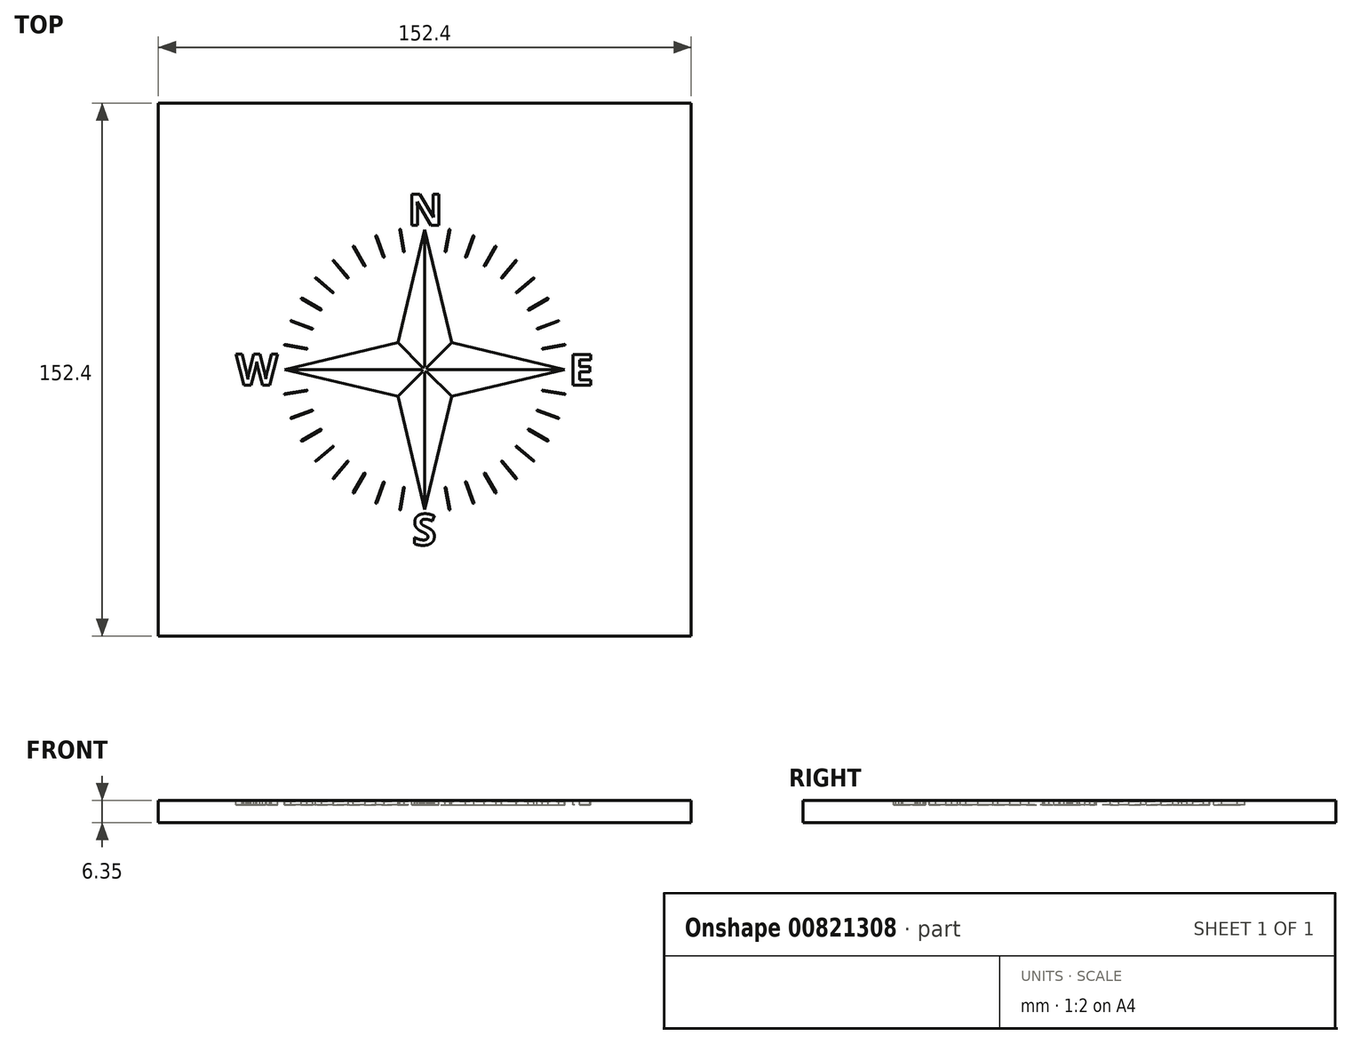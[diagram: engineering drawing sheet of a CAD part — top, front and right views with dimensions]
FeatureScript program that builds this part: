
annotation { "Feature Type Name" : "Feature", "Feature Type Description" : "" }
export const myFeature = defineFeature(function(context is Context, id is Id, definition is map)
    precondition{}
    {
        {
            var Q0;
            Q0=qCreatedBy(makeId("Top.planeOp"),FACE);
            var sketch = newSketch(context, id + "F0", { "sketchPlane" : qUnion([Q0])});
            skLineSegment(sketch, "E0.bottom", {"start": v(0, 0) * mm, "end": v(152.4, 0) * mm});
            skLineSegment(sketch, "E0.top", {"start": v(0, 152.4) * mm, "end": v(152.4, 152.4) * mm});
            skLineSegment(sketch, "E0.left", {"start": v(0, 0) * mm, "end": v(0, 152.4) * mm});
            skLineSegment(sketch, "E0.right", {"start": v(152.4, 0) * mm, "end": v(152.4, 152.4) * mm});
            skSolve(sketch);
        }
        {
            var Q0;
            Q0=makeQuery(id+"F0.imprint","IMPRINT",FACE,{"disambiguationData":[TD([[makeQuery(id+"F0.imprint","IMPRINT",EDGE,{"derivedFrom":sQuery(id+"F0.wireOp",EDGE,"E0.bottom")}),1.0]])]});
            extrude(context, id + "F1", {"entities" : qUnion([Q0]), "depth" : 6.35 * mm, "offsetDistance" : 25.4 * mm});
        }
        {
            var Q0;
            Q0=makeQuery(id+"F1.opExtrude","CAP_FACE",FACE,{"disambiguationData":[OSD([sQuery(id+"F0.wireOp",EDGE,"E0.bottom"),sQuery(id+"F0.wireOp",EDGE,"E0.top"),sQuery(id+"F0.wireOp",EDGE,"E0.left"),sQuery(id+"F0.wireOp",EDGE,"E0.right")])],"isStart":false});
            var sketch = newSketch(context, id + "F2", { "sketchPlane" : qUnion([Q0])});
            skCircle(sketch, "E1", {"center": v(76.2, 76.2) * mm, "radius": 38.1 * mm, "construction": true});
            skPoint(sketch, "E1.centerSnap0", {"position": v(76.2, 152.4) * mm});
            skPoint(sketch, "E1.centerSnap1", {"position": v(0, 76.2) * mm});
            skText(sketch, "E2", { "text": "N", "fontName": "OpenSans-Bold.ttf"});
            skText(sketch, "E3", { "text": "E", "fontName": "OpenSans-Bold.ttf"});
            skText(sketch, "E4", { "text": "S", "fontName": "OpenSans-Bold.ttf"});
            skText(sketch, "E5", { "text": "W", "fontName": "OpenSans-Bold.ttf"});
            skPoint(sketch, "E6", {"position": v(34.92, 76.2) * mm});
            skPoint(sketch, "E7", {"position": v(117.48, 76.2) * mm});
            const initialGuessF2  = {"E2": [0.07134, 0.11748, 1, 0, 0.0089], "E3": [0.11747, 0.07175, 1, 0, 0.00889], "E4": [0.07264, 0.02604, 1, 0, 0.0089], "E5": [0.02219, 0.07176, 1, 0, 0.00889]};
            skSetInitialGuess(sketch, initialGuessF2);
            skSolve(sketch);
        }
        {
            var Q0;
            Q0=makeQuery(id+"F2.imprint","IMPRINT",FACE,{"disambiguationData":[TD([[makeQuery(id+"F2.imprint","IMPRINT",EDGE,{"derivedFrom":sQuery(id+"F2.wireOp",EDGE,"E2.sketch_text.stroke-0")}),-1.0]])]});
            var Q1;
            Q1=makeQuery(id+"F2.imprint","IMPRINT",FACE,{"disambiguationData":[TD([[makeQuery(id+"F2.imprint","IMPRINT",EDGE,{"derivedFrom":sQuery(id+"F2.wireOp",EDGE,"E3.sketch_text.stroke-0")}),-1.0]])]});
            var Q2;
            Q2=makeQuery(id+"F2.imprint","IMPRINT",FACE,{"disambiguationData":[TD([[makeQuery(id+"F2.imprint","IMPRINT",EDGE,{"derivedFrom":sQuery(id+"F2.wireOp",EDGE,"E4.sketch_text.stroke-0")}),-1.0]])]});
            var Q3;
            Q3=makeQuery(id+"F2.imprint","IMPRINT",FACE,{"disambiguationData":[TD([[makeQuery(id+"F2.imprint","IMPRINT",EDGE,{"derivedFrom":sQuery(id+"F2.wireOp",EDGE,"E5.sketch_text.stroke-0")}),-1.0]])]});
            extrude(context, id + "F3", {"entities" : qUnion([Q0, Q1, Q2, Q3]), "operationType" : NewBodyOperationType.REMOVE, "oppositeDirection" : true, "depth" : 1.27 * mm, "offsetDistance" : 25.4 * mm});
        }
        {
            var Q0;
            Q0=makeQuery(id+"F1.opExtrude","CAP_FACE",FACE,{"disambiguationData":[OSD([sQuery(id+"F0.wireOp",EDGE,"E0.bottom"),sQuery(id+"F0.wireOp",EDGE,"E0.top"),sQuery(id+"F0.wireOp",EDGE,"E0.left"),sQuery(id+"F0.wireOp",EDGE,"E0.right")])],"isStart":false});
            var sketch = newSketch(context, id + "F4", { "sketchPlane" : qUnion([Q0])});
            skLineSegment(sketch, "E8", {"start": v(0, 76.2) * mm, "end": v(152.4, 76.2) * mm, "construction": true});
            skCircle(sketch, "E9", {"center": v(76.2, 76.2) * mm, "radius": 38.1 * mm, "construction": true});
            skCircle(sketch, "E10", {"center": v(76.2, 76.2) * mm, "radius": 40 * mm});
            skLineSegment(sketch, "E11", {"start": v(76.2, 116.2) * mm, "end": v(68.5, 83.9) * mm});
            skLineSegment(sketch, "E12", {"start": v(68.5, 68.5) * mm, "end": v(76.2, 36.2) * mm});
            skLineSegment(sketch, "E13", {"start": v(76.2, 36.2) * mm, "end": v(83.9, 68.5) * mm});
            skLineSegment(sketch, "E14", {"start": v(83.9, 83.9) * mm, "end": v(76.2, 116.2) * mm});
            skLineSegment(sketch, "E15", {"start": v(36.2, 76.2) * mm, "end": v(68.5, 83.9) * mm});
            skLineSegment(sketch, "E16", {"start": v(83.9, 83.9) * mm, "end": v(116.2, 76.2) * mm});
            skLineSegment(sketch, "E17", {"start": v(116.2, 76.2) * mm, "end": v(83.9, 68.5) * mm});
            skLineSegment(sketch, "E18", {"start": v(68.5, 68.5) * mm, "end": v(36.2, 76.2) * mm});
            skPoint(sketch, "E19.orphan", {"position": v(76.2, 85.72) * mm});
            skPoint(sketch, "E20.orphan", {"position": v(85.73, 76.2) * mm});
            skPoint(sketch, "E21.orphan", {"position": v(76.2, 66.67) * mm});
            skPoint(sketch, "E22.orphan", {"position": v(66.67, 76.2) * mm});
            skSolve(sketch);
        }
        {
            var Q0;
            Q0=makeQuery(id+"F4.imprint","IMPRINT",FACE,{"disambiguationData":[TD([[makeQuery(id+"F4.imprint","IMPRINT",EDGE,{"derivedFrom":sQuery(id+"F4.wireOp",EDGE,"E11")}),1.0]])]});
            extrude(context, id + "F5", {"entities" : qUnion([Q0]), "operationType" : NewBodyOperationType.REMOVE, "oppositeDirection" : true, "depth" : 1.27 * mm, "offsetDistance" : 25.4 * mm});
        }
        {
            var Q0;
            Q0=makeQuery(id+"F5.boolean.opBoolean","COPY",FACE,{"derivedFrom":makeQuery(id+"F5.opExtrude","CAP_FACE",FACE,{"disambiguationData":[OSD([sQuery(id+"F4.wireOp",EDGE,"E11"),sQuery(id+"F4.wireOp",EDGE,"E12"),sQuery(id+"F4.wireOp",EDGE,"E13"),sQuery(id+"F4.wireOp",EDGE,"E14"),sQuery(id+"F4.wireOp",EDGE,"E15"),sQuery(id+"F4.wireOp",EDGE,"E16"),sQuery(id+"F4.wireOp",EDGE,"E17"),sQuery(id+"F4.wireOp",EDGE,"E18")])],"isStart":false})});
            var sketch = newSketch(context, id + "F6", { "sketchPlane" : qUnion([Q0])});
            skLineSegment(sketch, "E23.0.0", {"start": v(68.5, 68.5) * mm, "end": v(76.2, 36.2) * mm});
            skLineSegment(sketch, "E23.0.1", {"start": v(76.2, 36.2) * mm, "end": v(83.9, 68.5) * mm});
            skLineSegment(sketch, "E23.0.2", {"start": v(83.9, 68.5) * mm, "end": v(116.2, 76.2) * mm});
            skLineSegment(sketch, "E23.0.3", {"start": v(116.2, 76.2) * mm, "end": v(83.9, 83.9) * mm});
            skLineSegment(sketch, "E23.0.4", {"start": v(83.9, 83.9) * mm, "end": v(76.2, 116.2) * mm});
            skLineSegment(sketch, "E23.0.5", {"start": v(76.2, 116.2) * mm, "end": v(68.5, 83.9) * mm});
            skLineSegment(sketch, "E23.0.6", {"start": v(68.5, 83.9) * mm, "end": v(36.2, 76.2) * mm});
            skLineSegment(sketch, "E23.0.7", {"start": v(36.2, 76.2) * mm, "end": v(68.5, 68.5) * mm});
            skLineSegment(sketch, "E24", {"start": v(76.2, 116.2) * mm, "end": v(76.2, 76.96) * mm});
            skLineSegment(sketch, "E25", {"start": v(36.2, 76.2) * mm, "end": v(75.44, 76.2) * mm});
            skLineSegment(sketch, "E26", {"start": v(68.5, 83.9) * mm, "end": v(75.66, 76.74) * mm});
            skLineSegment(sketch, "E27", {"start": v(83.9, 83.9) * mm, "end": v(76.74, 76.74) * mm});
            skCircle(sketch, "E28", {"center": v(76.2, 76.2) * mm, "radius": 0.76 * mm});
            skLineSegment(sketch, "E29.trimOffspring", {"start": v(76.74, 75.66) * mm, "end": v(83.9, 68.5) * mm});
            skLineSegment(sketch, "E30.trimOffspring", {"start": v(76.96, 76.2) * mm, "end": v(116.2, 76.2) * mm});
            skLineSegment(sketch, "E31.trimOffspring", {"start": v(75.66, 75.66) * mm, "end": v(68.5, 68.5) * mm});
            skLineSegment(sketch, "E32.trimOffspring", {"start": v(76.2, 75.44) * mm, "end": v(76.2, 36.2) * mm});
            skSolve(sketch);
        }
        {
            var Q0;
            Q0=makeQuery(id+"F6.imprint","IMPRINT",FACE,{"disambiguationData":[TD([[makeQuery(id+"F6.imprint","IMPRINT",EDGE,{"derivedFrom":sQuery(id+"F6.wireOp",EDGE,"E23.0.4")}),1.0]])]});
            var Q1;
            Q1=makeQuery(id+"F6.imprint","IMPRINT",FACE,{"disambiguationData":[TD([[makeQuery(id+"F6.imprint","IMPRINT",EDGE,{"derivedFrom":sQuery(id+"F6.wireOp",EDGE,"E23.0.6")}),-1.0]])]});
            var Q2;
            Q2=makeQuery(id+"F6.imprint","IMPRINT",FACE,{"disambiguationData":[TD([[makeQuery(id+"F6.imprint","IMPRINT",EDGE,{"derivedFrom":sQuery(id+"F6.wireOp",EDGE,"E23.0.0")}),1.0]])]});
            var Q3;
            Q3=makeQuery(id+"F6.imprint","IMPRINT",FACE,{"disambiguationData":[TD([[makeQuery(id+"F6.imprint","IMPRINT",EDGE,{"derivedFrom":sQuery(id+"F6.wireOp",EDGE,"E23.0.2")}),-1.0]])]});
            var Q4;
            {var subQ0=sQuery(id+"F6.wireOp",EDGE,"E28");var subQ4=makeQuery(id+"F6.imprint","INTERSECT",VERTEX,{"derivedFrom":[sQuery(id+"F6.wireOp",EDGE,"E27"),subQ0]});Q4=makeQuery(id+"F6.imprint","IMPRINT",FACE,{"disambiguationData":[TD([[makeQuery(id+"F6.imprint","IMPRINT",EDGE,{"disambiguationData":[TD([[subQ4,1.0]])],"derivedFrom":subQ0}),1.0]])]});}
            extrude(context, id + "F7", {"entities" : qUnion([Q0, Q1, Q2, Q3, Q4]), "operationType" : NewBodyOperationType.ADD, "depth" : 1.02 * mm, "offsetDistance" : 25.4 * mm});
        }
        {
            var Q0;
            Q0=makeQuery(id+"F1.opExtrude","CAP_FACE",FACE,{"disambiguationData":[OSD([sQuery(id+"F0.wireOp",EDGE,"E0.bottom"),sQuery(id+"F0.wireOp",EDGE,"E0.top"),sQuery(id+"F0.wireOp",EDGE,"E0.left"),sQuery(id+"F0.wireOp",EDGE,"E0.right")])],"isStart":false});
            var sketch = newSketch(context, id + "F8", { "sketchPlane" : qUnion([Q0])});
            skLineSegment(sketch, "E33.0", {"start": v(36.2, 76.2) * mm, "end": v(75.44, 76.2) * mm});
            skLineSegment(sketch, "E34.0", {"start": v(76.96, 76.2) * mm, "end": v(116.2, 76.2) * mm});
            skLineSegment(sketch, "E35.0", {"start": v(76.2, 75.44) * mm, "end": v(76.2, 36.2) * mm});
            skPoint(sketch, "E36", {"position": v(76.2, 76.2) * mm});
            skCircle(sketch, "E37", {"center": v(76.2, 76.2) * mm, "radius": 37.07 * mm, "construction": true});
            skCircle(sketch, "E38", {"center": v(76.2, 76.2) * mm, "radius": 37.84 * mm, "construction": true});
            skLineSegment(sketch, "E39", {"start": v(76.07, 110.48) * mm, "end": v(76.07, 116.83) * mm});
            skLineSegment(sketch, "E40", {"start": v(76.33, 110.48) * mm, "end": v(76.33, 116.83) * mm});
            skArc(sketch, "E41", {"start": v(76.33, 116.83) * mm, "mid": v(76.2, 116.96) * mm, "end": v(76.07, 116.83) * mm});
            skArc(sketch, "E42", {"start": v(76.07, 110.48) * mm, "mid": v(76.2, 110.35) * mm, "end": v(76.33, 110.48) * mm});
            skLineSegment(sketch, "E43", {"start": v(76.2, 113.27) * mm, "end": v(76.2, 114.04) * mm, "construction": true});
            skPoint(sketch, "E43.startSnap0", {"position": v(76.2, 110.35) * mm});
            skPoint(sketch, "E44", {"position": v(76.2, 113.65) * mm});
            skLineSegment(sketch, "E45.1.0", {"start": v(70.12, 109.94) * mm, "end": v(69.02, 116.19) * mm});
            skLineSegment(sketch, "E45.1.1", {"start": v(70.37, 109.98) * mm, "end": v(69.27, 116.23) * mm});
            skArc(sketch, "E45.1.2", {"start": v(70.12, 109.94) * mm, "mid": v(70.27, 109.83) * mm, "end": v(70.37, 109.98) * mm});
            skArc(sketch, "E45.1.3", {"start": v(69.27, 116.23) * mm, "mid": v(69.12, 116.34) * mm, "end": v(69.02, 116.19) * mm});
            skLineSegment(sketch, "E45.2.0", {"start": v(64.36, 108.37) * mm, "end": v(62.18, 114.34) * mm});
            skLineSegment(sketch, "E45.2.1", {"start": v(64.6, 108.46) * mm, "end": v(62.42, 114.42) * mm});
            skArc(sketch, "E45.2.2", {"start": v(64.36, 108.37) * mm, "mid": v(64.52, 108.3) * mm, "end": v(64.6, 108.46) * mm});
            skArc(sketch, "E45.2.3", {"start": v(62.42, 114.42) * mm, "mid": v(62.26, 114.5) * mm, "end": v(62.18, 114.34) * mm});
            skLineSegment(sketch, "E45.3.0", {"start": v(58.95, 105.82) * mm, "end": v(55.78, 111.32) * mm});
            skLineSegment(sketch, "E45.3.1", {"start": v(59.17, 105.95) * mm, "end": v(56, 111.45) * mm});
            skArc(sketch, "E45.3.2", {"start": v(58.95, 105.82) * mm, "mid": v(59.12, 105.78) * mm, "end": v(59.17, 105.95) * mm});
            skArc(sketch, "E45.3.3", {"start": v(56, 111.45) * mm, "mid": v(55.82, 111.5) * mm, "end": v(55.78, 111.32) * mm});
            skLineSegment(sketch, "E45.4.0", {"start": v(54.07, 102.38) * mm, "end": v(49.99, 107.24) * mm});
            skLineSegment(sketch, "E45.4.1", {"start": v(54.26, 102.54) * mm, "end": v(50.18, 107.4) * mm});
            skArc(sketch, "E45.4.2", {"start": v(54.07, 102.38) * mm, "mid": v(54.25, 102.36) * mm, "end": v(54.26, 102.54) * mm});
            skArc(sketch, "E45.4.3", {"start": v(50.18, 107.4) * mm, "mid": v(50, 107.42) * mm, "end": v(49.99, 107.24) * mm});
            skLineSegment(sketch, "E45.5.0", {"start": v(49.86, 98.14) * mm, "end": v(45, 102.22) * mm});
            skLineSegment(sketch, "E45.5.1", {"start": v(50.02, 98.33) * mm, "end": v(45.16, 102.41) * mm});
            skArc(sketch, "E45.5.2", {"start": v(49.86, 98.14) * mm, "mid": v(50.04, 98.15) * mm, "end": v(50.02, 98.33) * mm});
            skArc(sketch, "E45.5.3", {"start": v(45.16, 102.41) * mm, "mid": v(44.98, 102.4) * mm, "end": v(45, 102.22) * mm});
            skLineSegment(sketch, "E45.6.0", {"start": v(46.45, 93.23) * mm, "end": v(40.95, 96.4) * mm});
            skLineSegment(sketch, "E45.6.1", {"start": v(46.58, 93.45) * mm, "end": v(41.08, 96.62) * mm});
            skArc(sketch, "E45.6.2", {"start": v(46.45, 93.23) * mm, "mid": v(46.62, 93.28) * mm, "end": v(46.58, 93.45) * mm});
            skArc(sketch, "E45.6.3", {"start": v(41.08, 96.62) * mm, "mid": v(40.9, 96.58) * mm, "end": v(40.95, 96.4) * mm});
            skLineSegment(sketch, "E45.7.0", {"start": v(43.94, 87.8) * mm, "end": v(37.98, 89.98) * mm});
            skLineSegment(sketch, "E45.7.1", {"start": v(44.03, 88.04) * mm, "end": v(38.06, 90.22) * mm});
            skArc(sketch, "E45.7.2", {"start": v(43.94, 87.8) * mm, "mid": v(44.1, 87.88) * mm, "end": v(44.03, 88.04) * mm});
            skArc(sketch, "E45.7.3", {"start": v(38.06, 90.22) * mm, "mid": v(37.9, 90.14) * mm, "end": v(37.98, 89.98) * mm});
            skLineSegment(sketch, "E45.8.0", {"start": v(42.42, 82.03) * mm, "end": v(36.17, 83.13) * mm});
            skLineSegment(sketch, "E45.8.1", {"start": v(42.46, 82.28) * mm, "end": v(36.21, 83.38) * mm});
            skArc(sketch, "E45.8.2", {"start": v(42.42, 82.03) * mm, "mid": v(42.57, 82.13) * mm, "end": v(42.46, 82.28) * mm});
            skArc(sketch, "E45.8.3", {"start": v(36.21, 83.38) * mm, "mid": v(36.06, 83.28) * mm, "end": v(36.17, 83.13) * mm});
            skLineSegment(sketch, "E45.9.0", {"start": v(41.92, 76.07) * mm, "end": v(35.57, 76.07) * mm});
            skLineSegment(sketch, "E45.9.1", {"start": v(41.92, 76.33) * mm, "end": v(35.57, 76.33) * mm});
            skArc(sketch, "E45.9.2", {"start": v(41.92, 76.07) * mm, "mid": v(42.05, 76.2) * mm, "end": v(41.92, 76.33) * mm});
            skArc(sketch, "E45.9.3", {"start": v(35.57, 76.33) * mm, "mid": v(35.44, 76.2) * mm, "end": v(35.57, 76.07) * mm});
            skLineSegment(sketch, "E45.10.0", {"start": v(42.46, 70.12) * mm, "end": v(36.21, 69.02) * mm});
            skLineSegment(sketch, "E45.10.1", {"start": v(42.42, 70.37) * mm, "end": v(36.17, 69.27) * mm});
            skArc(sketch, "E45.10.2", {"start": v(42.46, 70.12) * mm, "mid": v(42.57, 70.27) * mm, "end": v(42.42, 70.37) * mm});
            skArc(sketch, "E45.10.3", {"start": v(36.17, 69.27) * mm, "mid": v(36.06, 69.12) * mm, "end": v(36.21, 69.02) * mm});
            skLineSegment(sketch, "E45.11.0", {"start": v(44.03, 64.36) * mm, "end": v(38.06, 62.18) * mm});
            skLineSegment(sketch, "E45.11.1", {"start": v(43.94, 64.6) * mm, "end": v(37.98, 62.42) * mm});
            skArc(sketch, "E45.11.2", {"start": v(44.03, 64.36) * mm, "mid": v(44.1, 64.52) * mm, "end": v(43.94, 64.6) * mm});
            skArc(sketch, "E45.11.3", {"start": v(37.98, 62.42) * mm, "mid": v(37.9, 62.26) * mm, "end": v(38.06, 62.18) * mm});
            skLineSegment(sketch, "E45.12.0", {"start": v(46.58, 58.95) * mm, "end": v(41.08, 55.78) * mm});
            skLineSegment(sketch, "E45.12.1", {"start": v(46.45, 59.17) * mm, "end": v(40.95, 56) * mm});
            skArc(sketch, "E45.12.2", {"start": v(46.58, 58.95) * mm, "mid": v(46.62, 59.12) * mm, "end": v(46.45, 59.17) * mm});
            skArc(sketch, "E45.12.3", {"start": v(40.95, 56) * mm, "mid": v(40.9, 55.82) * mm, "end": v(41.08, 55.78) * mm});
            skLineSegment(sketch, "E45.13.0", {"start": v(50.02, 54.07) * mm, "end": v(45.16, 49.99) * mm});
            skLineSegment(sketch, "E45.13.1", {"start": v(49.86, 54.26) * mm, "end": v(45, 50.18) * mm});
            skArc(sketch, "E45.13.2", {"start": v(50.02, 54.07) * mm, "mid": v(50.04, 54.25) * mm, "end": v(49.86, 54.26) * mm});
            skArc(sketch, "E45.13.3", {"start": v(45, 50.18) * mm, "mid": v(44.98, 50) * mm, "end": v(45.16, 49.99) * mm});
            skLineSegment(sketch, "E45.14.0", {"start": v(54.26, 49.86) * mm, "end": v(50.18, 45) * mm});
            skLineSegment(sketch, "E45.14.1", {"start": v(54.07, 50.02) * mm, "end": v(49.99, 45.16) * mm});
            skArc(sketch, "E45.14.2", {"start": v(54.26, 49.86) * mm, "mid": v(54.25, 50.04) * mm, "end": v(54.07, 50.02) * mm});
            skArc(sketch, "E45.14.3", {"start": v(49.99, 45.16) * mm, "mid": v(50, 44.98) * mm, "end": v(50.18, 45) * mm});
            skLineSegment(sketch, "E45.15.0", {"start": v(59.17, 46.45) * mm, "end": v(56, 40.95) * mm});
            skLineSegment(sketch, "E45.15.1", {"start": v(58.95, 46.58) * mm, "end": v(55.78, 41.08) * mm});
            skArc(sketch, "E45.15.2", {"start": v(59.17, 46.45) * mm, "mid": v(59.12, 46.62) * mm, "end": v(58.95, 46.58) * mm});
            skArc(sketch, "E45.15.3", {"start": v(55.78, 41.08) * mm, "mid": v(55.82, 40.9) * mm, "end": v(56, 40.95) * mm});
            skLineSegment(sketch, "E45.16.0", {"start": v(64.6, 43.94) * mm, "end": v(62.42, 37.98) * mm});
            skLineSegment(sketch, "E45.16.1", {"start": v(64.36, 44.03) * mm, "end": v(62.18, 38.06) * mm});
            skArc(sketch, "E45.16.2", {"start": v(64.6, 43.94) * mm, "mid": v(64.52, 44.1) * mm, "end": v(64.36, 44.03) * mm});
            skArc(sketch, "E45.16.3", {"start": v(62.18, 38.06) * mm, "mid": v(62.26, 37.9) * mm, "end": v(62.42, 37.98) * mm});
            skLineSegment(sketch, "E45.17.0", {"start": v(70.37, 42.42) * mm, "end": v(69.27, 36.17) * mm});
            skLineSegment(sketch, "E45.17.1", {"start": v(70.12, 42.46) * mm, "end": v(69.02, 36.21) * mm});
            skArc(sketch, "E45.17.2", {"start": v(70.37, 42.42) * mm, "mid": v(70.27, 42.57) * mm, "end": v(70.12, 42.46) * mm});
            skArc(sketch, "E45.17.3", {"start": v(69.02, 36.21) * mm, "mid": v(69.12, 36.06) * mm, "end": v(69.27, 36.17) * mm});
            skLineSegment(sketch, "E45.18.0", {"start": v(76.33, 41.92) * mm, "end": v(76.33, 35.57) * mm});
            skLineSegment(sketch, "E45.18.1", {"start": v(76.07, 41.92) * mm, "end": v(76.07, 35.57) * mm});
            skArc(sketch, "E45.18.2", {"start": v(76.33, 41.92) * mm, "mid": v(76.2, 42.05) * mm, "end": v(76.07, 41.92) * mm});
            skArc(sketch, "E45.18.3", {"start": v(76.07, 35.57) * mm, "mid": v(76.2, 35.44) * mm, "end": v(76.33, 35.57) * mm});
            skLineSegment(sketch, "E45.19.0", {"start": v(82.28, 42.46) * mm, "end": v(83.38, 36.21) * mm});
            skLineSegment(sketch, "E45.19.1", {"start": v(82.03, 42.42) * mm, "end": v(83.13, 36.17) * mm});
            skArc(sketch, "E45.19.2", {"start": v(82.28, 42.46) * mm, "mid": v(82.13, 42.57) * mm, "end": v(82.03, 42.42) * mm});
            skArc(sketch, "E45.19.3", {"start": v(83.13, 36.17) * mm, "mid": v(83.28, 36.06) * mm, "end": v(83.38, 36.21) * mm});
            skLineSegment(sketch, "E45.20.0", {"start": v(88.04, 44.03) * mm, "end": v(90.22, 38.06) * mm});
            skLineSegment(sketch, "E45.20.1", {"start": v(87.8, 43.94) * mm, "end": v(89.98, 37.98) * mm});
            skArc(sketch, "E45.20.2", {"start": v(88.04, 44.03) * mm, "mid": v(87.88, 44.1) * mm, "end": v(87.8, 43.94) * mm});
            skArc(sketch, "E45.20.3", {"start": v(89.98, 37.98) * mm, "mid": v(90.14, 37.9) * mm, "end": v(90.22, 38.06) * mm});
            skLineSegment(sketch, "E45.21.0", {"start": v(93.45, 46.58) * mm, "end": v(96.62, 41.08) * mm});
            skLineSegment(sketch, "E45.21.1", {"start": v(93.23, 46.45) * mm, "end": v(96.4, 40.95) * mm});
            skArc(sketch, "E45.21.2", {"start": v(93.45, 46.58) * mm, "mid": v(93.28, 46.62) * mm, "end": v(93.23, 46.45) * mm});
            skArc(sketch, "E45.21.3", {"start": v(96.4, 40.95) * mm, "mid": v(96.58, 40.9) * mm, "end": v(96.62, 41.08) * mm});
            skLineSegment(sketch, "E45.22.0", {"start": v(98.33, 50.02) * mm, "end": v(102.41, 45.16) * mm});
            skLineSegment(sketch, "E45.22.1", {"start": v(98.14, 49.86) * mm, "end": v(102.22, 45) * mm});
            skArc(sketch, "E45.22.2", {"start": v(98.33, 50.02) * mm, "mid": v(98.15, 50.04) * mm, "end": v(98.14, 49.86) * mm});
            skArc(sketch, "E45.22.3", {"start": v(102.22, 45) * mm, "mid": v(102.4, 44.98) * mm, "end": v(102.41, 45.16) * mm});
            skLineSegment(sketch, "E45.23.0", {"start": v(102.54, 54.26) * mm, "end": v(107.4, 50.18) * mm});
            skLineSegment(sketch, "E45.23.1", {"start": v(102.38, 54.07) * mm, "end": v(107.24, 49.99) * mm});
            skArc(sketch, "E45.23.2", {"start": v(102.54, 54.26) * mm, "mid": v(102.36, 54.25) * mm, "end": v(102.38, 54.07) * mm});
            skArc(sketch, "E45.23.3", {"start": v(107.24, 49.99) * mm, "mid": v(107.42, 50) * mm, "end": v(107.4, 50.18) * mm});
            skLineSegment(sketch, "E45.24.0", {"start": v(105.95, 59.17) * mm, "end": v(111.45, 56) * mm});
            skLineSegment(sketch, "E45.24.1", {"start": v(105.82, 58.95) * mm, "end": v(111.32, 55.78) * mm});
            skArc(sketch, "E45.24.2", {"start": v(105.95, 59.17) * mm, "mid": v(105.78, 59.12) * mm, "end": v(105.82, 58.95) * mm});
            skArc(sketch, "E45.24.3", {"start": v(111.32, 55.78) * mm, "mid": v(111.5, 55.82) * mm, "end": v(111.45, 56) * mm});
            skLineSegment(sketch, "E45.25.0", {"start": v(108.46, 64.6) * mm, "end": v(114.42, 62.42) * mm});
            skLineSegment(sketch, "E45.25.1", {"start": v(108.37, 64.36) * mm, "end": v(114.34, 62.18) * mm});
            skArc(sketch, "E45.25.2", {"start": v(108.46, 64.6) * mm, "mid": v(108.3, 64.52) * mm, "end": v(108.37, 64.36) * mm});
            skArc(sketch, "E45.25.3", {"start": v(114.34, 62.18) * mm, "mid": v(114.5, 62.26) * mm, "end": v(114.42, 62.42) * mm});
            skLineSegment(sketch, "E45.26.0", {"start": v(109.98, 70.37) * mm, "end": v(116.23, 69.27) * mm});
            skLineSegment(sketch, "E45.26.1", {"start": v(109.94, 70.12) * mm, "end": v(116.19, 69.02) * mm});
            skArc(sketch, "E45.26.2", {"start": v(109.98, 70.37) * mm, "mid": v(109.83, 70.27) * mm, "end": v(109.94, 70.12) * mm});
            skArc(sketch, "E45.26.3", {"start": v(116.19, 69.02) * mm, "mid": v(116.34, 69.12) * mm, "end": v(116.23, 69.27) * mm});
            skLineSegment(sketch, "E45.27.0", {"start": v(110.48, 76.33) * mm, "end": v(116.83, 76.33) * mm});
            skLineSegment(sketch, "E45.27.1", {"start": v(110.48, 76.07) * mm, "end": v(116.83, 76.07) * mm});
            skArc(sketch, "E45.27.2", {"start": v(110.48, 76.33) * mm, "mid": v(110.35, 76.2) * mm, "end": v(110.48, 76.07) * mm});
            skArc(sketch, "E45.27.3", {"start": v(116.83, 76.07) * mm, "mid": v(116.96, 76.2) * mm, "end": v(116.83, 76.33) * mm});
            skLineSegment(sketch, "E45.28.0", {"start": v(109.94, 82.28) * mm, "end": v(116.19, 83.38) * mm});
            skLineSegment(sketch, "E45.28.1", {"start": v(109.98, 82.03) * mm, "end": v(116.23, 83.13) * mm});
            skArc(sketch, "E45.28.2", {"start": v(109.94, 82.28) * mm, "mid": v(109.83, 82.13) * mm, "end": v(109.98, 82.03) * mm});
            skArc(sketch, "E45.28.3", {"start": v(116.23, 83.13) * mm, "mid": v(116.34, 83.28) * mm, "end": v(116.19, 83.38) * mm});
            skLineSegment(sketch, "E45.29.0", {"start": v(108.37, 88.04) * mm, "end": v(114.34, 90.22) * mm});
            skLineSegment(sketch, "E45.29.1", {"start": v(108.46, 87.8) * mm, "end": v(114.42, 89.98) * mm});
            skArc(sketch, "E45.29.2", {"start": v(108.37, 88.04) * mm, "mid": v(108.3, 87.88) * mm, "end": v(108.46, 87.8) * mm});
            skArc(sketch, "E45.29.3", {"start": v(114.42, 89.98) * mm, "mid": v(114.5, 90.14) * mm, "end": v(114.34, 90.22) * mm});
            skLineSegment(sketch, "E45.30.0", {"start": v(105.82, 93.45) * mm, "end": v(111.32, 96.62) * mm});
            skLineSegment(sketch, "E45.30.1", {"start": v(105.95, 93.23) * mm, "end": v(111.45, 96.4) * mm});
            skArc(sketch, "E45.30.2", {"start": v(105.82, 93.45) * mm, "mid": v(105.78, 93.28) * mm, "end": v(105.95, 93.23) * mm});
            skArc(sketch, "E45.30.3", {"start": v(111.45, 96.4) * mm, "mid": v(111.5, 96.58) * mm, "end": v(111.32, 96.62) * mm});
            skLineSegment(sketch, "E45.31.0", {"start": v(102.38, 98.33) * mm, "end": v(107.24, 102.41) * mm});
            skLineSegment(sketch, "E45.31.1", {"start": v(102.54, 98.14) * mm, "end": v(107.4, 102.22) * mm});
            skArc(sketch, "E45.31.2", {"start": v(102.38, 98.33) * mm, "mid": v(102.36, 98.15) * mm, "end": v(102.54, 98.14) * mm});
            skArc(sketch, "E45.31.3", {"start": v(107.4, 102.22) * mm, "mid": v(107.42, 102.4) * mm, "end": v(107.24, 102.41) * mm});
            skLineSegment(sketch, "E45.32.0", {"start": v(98.14, 102.54) * mm, "end": v(102.22, 107.4) * mm});
            skLineSegment(sketch, "E45.32.1", {"start": v(98.33, 102.38) * mm, "end": v(102.41, 107.24) * mm});
            skArc(sketch, "E45.32.2", {"start": v(98.14, 102.54) * mm, "mid": v(98.15, 102.36) * mm, "end": v(98.33, 102.38) * mm});
            skArc(sketch, "E45.32.3", {"start": v(102.41, 107.24) * mm, "mid": v(102.4, 107.42) * mm, "end": v(102.22, 107.4) * mm});
            skLineSegment(sketch, "E45.33.0", {"start": v(93.23, 105.95) * mm, "end": v(96.4, 111.45) * mm});
            skLineSegment(sketch, "E45.33.1", {"start": v(93.45, 105.82) * mm, "end": v(96.62, 111.32) * mm});
            skArc(sketch, "E45.33.2", {"start": v(93.23, 105.95) * mm, "mid": v(93.28, 105.78) * mm, "end": v(93.45, 105.82) * mm});
            skArc(sketch, "E45.33.3", {"start": v(96.62, 111.32) * mm, "mid": v(96.58, 111.5) * mm, "end": v(96.4, 111.45) * mm});
            skLineSegment(sketch, "E45.34.0", {"start": v(87.8, 108.46) * mm, "end": v(89.98, 114.42) * mm});
            skLineSegment(sketch, "E45.34.1", {"start": v(88.04, 108.37) * mm, "end": v(90.22, 114.34) * mm});
            skArc(sketch, "E45.34.2", {"start": v(87.8, 108.46) * mm, "mid": v(87.88, 108.3) * mm, "end": v(88.04, 108.37) * mm});
            skArc(sketch, "E45.34.3", {"start": v(90.22, 114.34) * mm, "mid": v(90.14, 114.5) * mm, "end": v(89.98, 114.42) * mm});
            skLineSegment(sketch, "E45.35.0", {"start": v(82.03, 109.98) * mm, "end": v(83.13, 116.23) * mm});
            skLineSegment(sketch, "E45.35.1", {"start": v(82.28, 109.94) * mm, "end": v(83.38, 116.19) * mm});
            skArc(sketch, "E45.35.2", {"start": v(82.03, 109.98) * mm, "mid": v(82.13, 109.83) * mm, "end": v(82.28, 109.94) * mm});
            skArc(sketch, "E45.35.3", {"start": v(83.38, 116.19) * mm, "mid": v(83.28, 116.34) * mm, "end": v(83.13, 116.23) * mm});
            skSolve(sketch);
        }
        {
            var Q0;
            Q0=makeQuery(id+"F8.imprint","IMPRINT",FACE,{"disambiguationData":[TD([[makeQuery(id+"F8.imprint","IMPRINT",EDGE,{"derivedFrom":sQuery(id+"F8.wireOp",EDGE,"E45.35.0")}),-1.0]])]});
            var Q1;
            Q1=makeQuery(id+"F8.imprint","IMPRINT",FACE,{"disambiguationData":[TD([[makeQuery(id+"F8.imprint","IMPRINT",EDGE,{"derivedFrom":sQuery(id+"F8.wireOp",EDGE,"E45.34.0")}),-1.0]])]});
            var Q2;
            Q2=makeQuery(id+"F8.imprint","IMPRINT",FACE,{"disambiguationData":[TD([[makeQuery(id+"F8.imprint","IMPRINT",EDGE,{"derivedFrom":sQuery(id+"F8.wireOp",EDGE,"E45.33.0")}),-1.0]])]});
            var Q3;
            Q3=makeQuery(id+"F8.imprint","IMPRINT",FACE,{"disambiguationData":[TD([[makeQuery(id+"F8.imprint","IMPRINT",EDGE,{"derivedFrom":sQuery(id+"F8.wireOp",EDGE,"E45.32.0")}),-1.0]])]});
            var Q4;
            Q4=makeQuery(id+"F8.imprint","IMPRINT",FACE,{"disambiguationData":[TD([[makeQuery(id+"F8.imprint","IMPRINT",EDGE,{"derivedFrom":sQuery(id+"F8.wireOp",EDGE,"E45.31.0")}),-1.0]])]});
            var Q5;
            Q5=makeQuery(id+"F8.imprint","IMPRINT",FACE,{"disambiguationData":[TD([[makeQuery(id+"F8.imprint","IMPRINT",EDGE,{"derivedFrom":sQuery(id+"F8.wireOp",EDGE,"E45.30.0")}),-1.0]])]});
            var Q6;
            Q6=makeQuery(id+"F8.imprint","IMPRINT",FACE,{"disambiguationData":[TD([[makeQuery(id+"F8.imprint","IMPRINT",EDGE,{"derivedFrom":sQuery(id+"F8.wireOp",EDGE,"E45.29.0")}),-1.0]])]});
            var Q7;
            Q7=makeQuery(id+"F8.imprint","IMPRINT",FACE,{"disambiguationData":[TD([[makeQuery(id+"F8.imprint","IMPRINT",EDGE,{"derivedFrom":sQuery(id+"F8.wireOp",EDGE,"E45.28.0")}),-1.0]])]});
            var Q8;
            Q8=makeQuery(id+"F8.imprint","IMPRINT",FACE,{"disambiguationData":[TD([[makeQuery(id+"F8.imprint","IMPRINT",EDGE,{"derivedFrom":sQuery(id+"F8.wireOp",EDGE,"E45.26.0")}),-1.0]])]});
            var Q9;
            Q9=makeQuery(id+"F8.imprint","IMPRINT",FACE,{"disambiguationData":[TD([[makeQuery(id+"F8.imprint","IMPRINT",EDGE,{"derivedFrom":sQuery(id+"F8.wireOp",EDGE,"E45.25.0")}),-1.0]])]});
            var Q10;
            Q10=makeQuery(id+"F8.imprint","IMPRINT",FACE,{"disambiguationData":[TD([[makeQuery(id+"F8.imprint","IMPRINT",EDGE,{"derivedFrom":sQuery(id+"F8.wireOp",EDGE,"E45.24.0")}),-1.0]])]});
            var Q11;
            Q11=makeQuery(id+"F8.imprint","IMPRINT",FACE,{"disambiguationData":[TD([[makeQuery(id+"F8.imprint","IMPRINT",EDGE,{"derivedFrom":sQuery(id+"F8.wireOp",EDGE,"E45.23.0")}),-1.0]])]});
            var Q12;
            Q12=makeQuery(id+"F8.imprint","IMPRINT",FACE,{"disambiguationData":[TD([[makeQuery(id+"F8.imprint","IMPRINT",EDGE,{"derivedFrom":sQuery(id+"F8.wireOp",EDGE,"E45.22.0")}),-1.0]])]});
            var Q13;
            Q13=makeQuery(id+"F8.imprint","IMPRINT",FACE,{"disambiguationData":[TD([[makeQuery(id+"F8.imprint","IMPRINT",EDGE,{"derivedFrom":sQuery(id+"F8.wireOp",EDGE,"E45.21.0")}),-1.0]])]});
            var Q14;
            Q14=makeQuery(id+"F8.imprint","IMPRINT",FACE,{"disambiguationData":[TD([[makeQuery(id+"F8.imprint","IMPRINT",EDGE,{"derivedFrom":sQuery(id+"F8.wireOp",EDGE,"E45.20.0")}),-1.0]])]});
            var Q15;
            Q15=makeQuery(id+"F8.imprint","IMPRINT",FACE,{"disambiguationData":[TD([[makeQuery(id+"F8.imprint","IMPRINT",EDGE,{"derivedFrom":sQuery(id+"F8.wireOp",EDGE,"E45.19.0")}),-1.0]])]});
            var Q16;
            Q16=makeQuery(id+"F8.imprint","IMPRINT",FACE,{"disambiguationData":[TD([[makeQuery(id+"F8.imprint","IMPRINT",EDGE,{"derivedFrom":sQuery(id+"F8.wireOp",EDGE,"E45.17.0")}),-1.0]])]});
            var Q17;
            Q17=makeQuery(id+"F8.imprint","IMPRINT",FACE,{"disambiguationData":[TD([[makeQuery(id+"F8.imprint","IMPRINT",EDGE,{"derivedFrom":sQuery(id+"F8.wireOp",EDGE,"E45.16.0")}),-1.0]])]});
            var Q18;
            Q18=makeQuery(id+"F8.imprint","IMPRINT",FACE,{"disambiguationData":[TD([[makeQuery(id+"F8.imprint","IMPRINT",EDGE,{"derivedFrom":sQuery(id+"F8.wireOp",EDGE,"E45.15.0")}),-1.0]])]});
            var Q19;
            Q19=makeQuery(id+"F8.imprint","IMPRINT",FACE,{"disambiguationData":[TD([[makeQuery(id+"F8.imprint","IMPRINT",EDGE,{"derivedFrom":sQuery(id+"F8.wireOp",EDGE,"E45.14.0")}),-1.0]])]});
            var Q20;
            Q20=makeQuery(id+"F8.imprint","IMPRINT",FACE,{"disambiguationData":[TD([[makeQuery(id+"F8.imprint","IMPRINT",EDGE,{"derivedFrom":sQuery(id+"F8.wireOp",EDGE,"E45.13.0")}),-1.0]])]});
            var Q21;
            Q21=makeQuery(id+"F8.imprint","IMPRINT",FACE,{"disambiguationData":[TD([[makeQuery(id+"F8.imprint","IMPRINT",EDGE,{"derivedFrom":sQuery(id+"F8.wireOp",EDGE,"E45.12.0")}),-1.0]])]});
            var Q22;
            Q22=makeQuery(id+"F8.imprint","IMPRINT",FACE,{"disambiguationData":[TD([[makeQuery(id+"F8.imprint","IMPRINT",EDGE,{"derivedFrom":sQuery(id+"F8.wireOp",EDGE,"E45.11.0")}),-1.0]])]});
            var Q23;
            Q23=makeQuery(id+"F8.imprint","IMPRINT",FACE,{"disambiguationData":[TD([[makeQuery(id+"F8.imprint","IMPRINT",EDGE,{"derivedFrom":sQuery(id+"F8.wireOp",EDGE,"E45.10.0")}),-1.0]])]});
            var Q24;
            Q24=makeQuery(id+"F8.imprint","IMPRINT",FACE,{"disambiguationData":[TD([[makeQuery(id+"F8.imprint","IMPRINT",EDGE,{"derivedFrom":sQuery(id+"F8.wireOp",EDGE,"E45.8.0")}),-1.0]])]});
            var Q25;
            Q25=makeQuery(id+"F8.imprint","IMPRINT",FACE,{"disambiguationData":[TD([[makeQuery(id+"F8.imprint","IMPRINT",EDGE,{"derivedFrom":sQuery(id+"F8.wireOp",EDGE,"E45.7.0")}),-1.0]])]});
            var Q26;
            Q26=makeQuery(id+"F8.imprint","IMPRINT",FACE,{"disambiguationData":[TD([[makeQuery(id+"F8.imprint","IMPRINT",EDGE,{"derivedFrom":sQuery(id+"F8.wireOp",EDGE,"E45.6.0")}),-1.0]])]});
            var Q27;
            Q27=makeQuery(id+"F8.imprint","IMPRINT",FACE,{"disambiguationData":[TD([[makeQuery(id+"F8.imprint","IMPRINT",EDGE,{"derivedFrom":sQuery(id+"F8.wireOp",EDGE,"E45.5.0")}),-1.0]])]});
            var Q28;
            Q28=makeQuery(id+"F8.imprint","IMPRINT",FACE,{"disambiguationData":[TD([[makeQuery(id+"F8.imprint","IMPRINT",EDGE,{"derivedFrom":sQuery(id+"F8.wireOp",EDGE,"E45.4.0")}),-1.0]])]});
            var Q29;
            Q29=makeQuery(id+"F8.imprint","IMPRINT",FACE,{"disambiguationData":[TD([[makeQuery(id+"F8.imprint","IMPRINT",EDGE,{"derivedFrom":sQuery(id+"F8.wireOp",EDGE,"E45.3.0")}),-1.0]])]});
            var Q30;
            Q30=makeQuery(id+"F8.imprint","IMPRINT",FACE,{"disambiguationData":[TD([[makeQuery(id+"F8.imprint","IMPRINT",EDGE,{"derivedFrom":sQuery(id+"F8.wireOp",EDGE,"E45.2.0")}),-1.0]])]});
            var Q31;
            Q31=makeQuery(id+"F8.imprint","IMPRINT",FACE,{"disambiguationData":[TD([[makeQuery(id+"F8.imprint","IMPRINT",EDGE,{"derivedFrom":sQuery(id+"F8.wireOp",EDGE,"E45.1.0")}),-1.0]])]});
            extrude(context, id + "F9", {"entities" : qUnion([Q0, Q1, Q2, Q3, Q4, Q5, Q6, Q7, Q8, Q9, Q10, Q11, Q12, Q13, Q14, Q15, Q16, Q17, Q18, Q19, Q20, Q21, Q22, Q23, Q24, Q25, Q26, Q27, Q28, Q29, Q30, Q31]), "operationType" : NewBodyOperationType.REMOVE, "oppositeDirection" : true, "depth" : 1.27 * mm, "offsetDistance" : 25.4 * mm});
        }
    });
